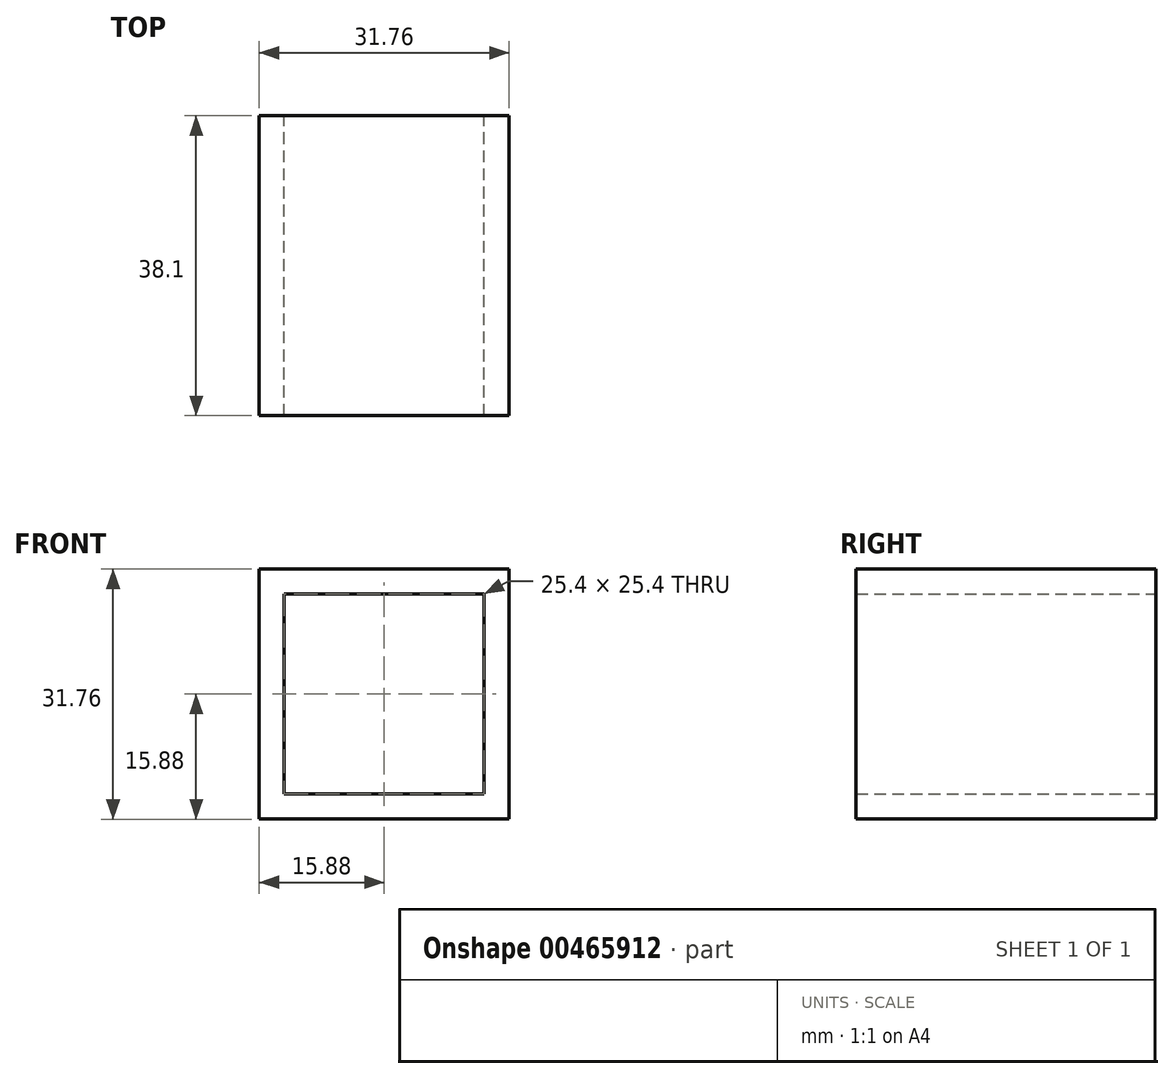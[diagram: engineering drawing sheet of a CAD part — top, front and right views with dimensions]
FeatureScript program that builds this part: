
annotation { "Feature Type Name" : "Feature", "Feature Type Description" : "" }
export const myFeature = defineFeature(function(context is Context, id is Id, definition is map)
    precondition{}
    {
        {
            var Q0;
            Q0=qCreatedBy(makeId("Front.planeOp"),FACE);
            var sketch = newSketch(context, id + "F0", { "sketchPlane" : qUnion([Q0])});
            skLineSegment(sketch, "E0.bottom", {"start": v(-15.88, 15.88) * mm, "end": v(15.88, 15.88) * mm});
            skLineSegment(sketch, "E0.top", {"start": v(-15.88, -15.88) * mm, "end": v(15.87, -15.88) * mm});
            skLineSegment(sketch, "E0.left", {"start": v(-15.88, 15.88) * mm, "end": v(-15.88, -15.87) * mm});
            skLineSegment(sketch, "E0.right", {"start": v(15.88, 15.88) * mm, "end": v(15.87, -15.88) * mm});
            skPoint(sketch, "E0.middle", {"position": v(0, 0) * mm});
            skLineSegment(sketch, "E1.bottom", {"start": v(-12.7, 12.7) * mm, "end": v(12.7, 12.7) * mm});
            skLineSegment(sketch, "E1.top", {"start": v(-12.7, -12.7) * mm, "end": v(12.7, -12.7) * mm});
            skLineSegment(sketch, "E1.left", {"start": v(-12.7, 12.7) * mm, "end": v(-12.7, -12.7) * mm});
            skLineSegment(sketch, "E1.right", {"start": v(12.7, 12.7) * mm, "end": v(12.7, -12.7) * mm});
            skSolve(sketch);
        }
        {
            var Q0;
            Q0=makeQuery(id+"F0.imprint","IMPRINT",FACE,{"disambiguationData":[TD([[makeQuery(id+"F0.imprint","IMPRINT",EDGE,{"derivedFrom":sQuery(id+"F0.wireOp",EDGE,"E0.bottom")}),-1.0]])]});
            extrude(context, id + "F1", {"entities" : qUnion([Q0]), "depth" : 38.1 * mm});
        }
    });
